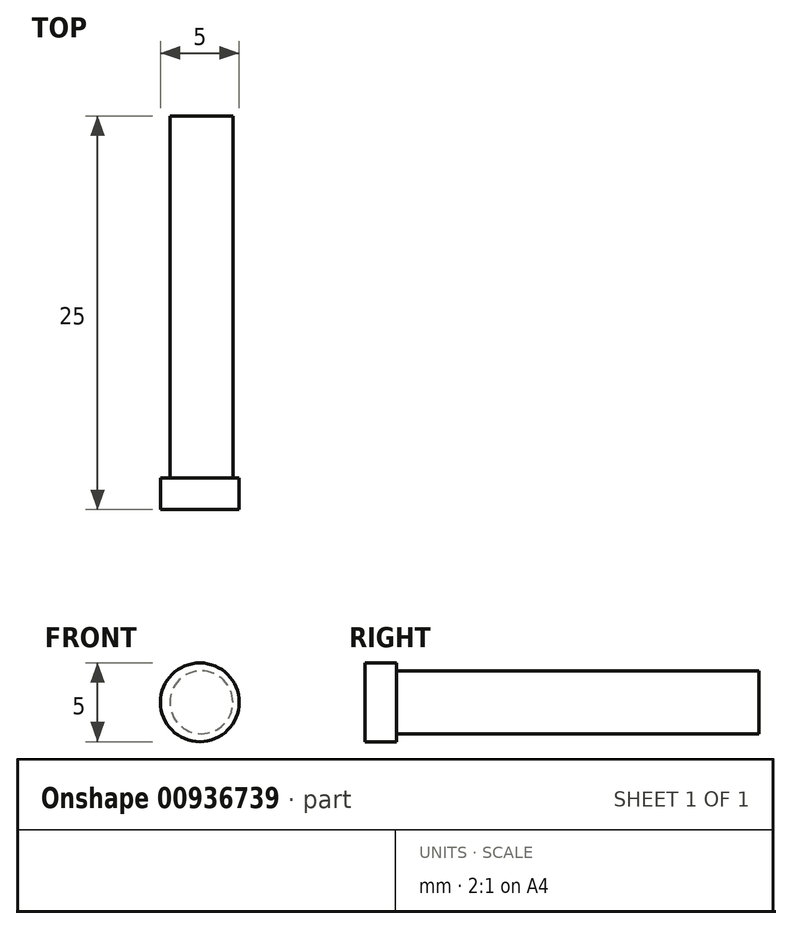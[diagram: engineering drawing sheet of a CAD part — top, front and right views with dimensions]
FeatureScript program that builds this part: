
annotation { "Feature Type Name" : "Feature", "Feature Type Description" : "" }
export const myFeature = defineFeature(function(context is Context, id is Id, definition is map)
    precondition{}
    {
        {
            var Q0;
            Q0=qCreatedBy(makeId("Front.planeOp"),FACE);
            var sketch = newSketch(context, id + "F0", { "sketchPlane" : qUnion([Q0])});
            skCircle(sketch, "E0", {"center": v(0, 0) * mm, "radius": 2 * mm});
            skSolve(sketch);
        }
        {
            var Q0;
            Q0=makeQuery(id+"F0.imprint","IMPRINT",FACE,{"disambiguationData":[TD([[makeQuery(id+"F0.imprint","IMPRINT",EDGE,{"derivedFrom":sQuery(id+"F0.wireOp",EDGE,"E0")}),1.0]])]});
            extrude(context, id + "F1", {"entities" : qUnion([Q0]), "depth" : 23 * mm, "offsetDistance" : 25 * mm});
        }
        {
            var Q0;
            Q0=makeQuery(id+"F1.opExtrude","CAP_FACE",FACE,{"disambiguationData":[OSD([sQuery(id+"F0.wireOp",EDGE,"E0")])],"isStart":false});
            var sketch = newSketch(context, id + "F2", { "sketchPlane" : qUnion([Q0])});
            skCircle(sketch, "E1", {"center": v(-0.1, 0) * mm, "radius": 2.5 * mm});
            skSolve(sketch);
        }
        {
            var Q0;
            Q0=makeQuery(id+"F2.imprint","IMPRINT",FACE,{"disambiguationData":[TD([[makeQuery(id+"F2.imprint","IMPRINT",EDGE,{"derivedFrom":makeQuery(id+"F1.opExtrude","CAP_EDGE",EDGE,{"disambiguationData":[OSD([sQuery(id+"F0.wireOp",EDGE,"E0")])],"isStart":false})}),1.0]])]});
            var Q1;
            Q1=makeQuery(id+"F2.imprint","IMPRINT",FACE,{"disambiguationData":[TD([[makeQuery(id+"F2.imprint","IMPRINT",EDGE,{"derivedFrom":sQuery(id+"F2.wireOp",EDGE,"E1")}),1.0]])]});
            extrude(context, id + "F3", {"entities" : qUnion([Q0, Q1]), "operationType" : NewBodyOperationType.ADD, "depth" : 2 * mm, "offsetDistance" : 25 * mm});
        }
    });
